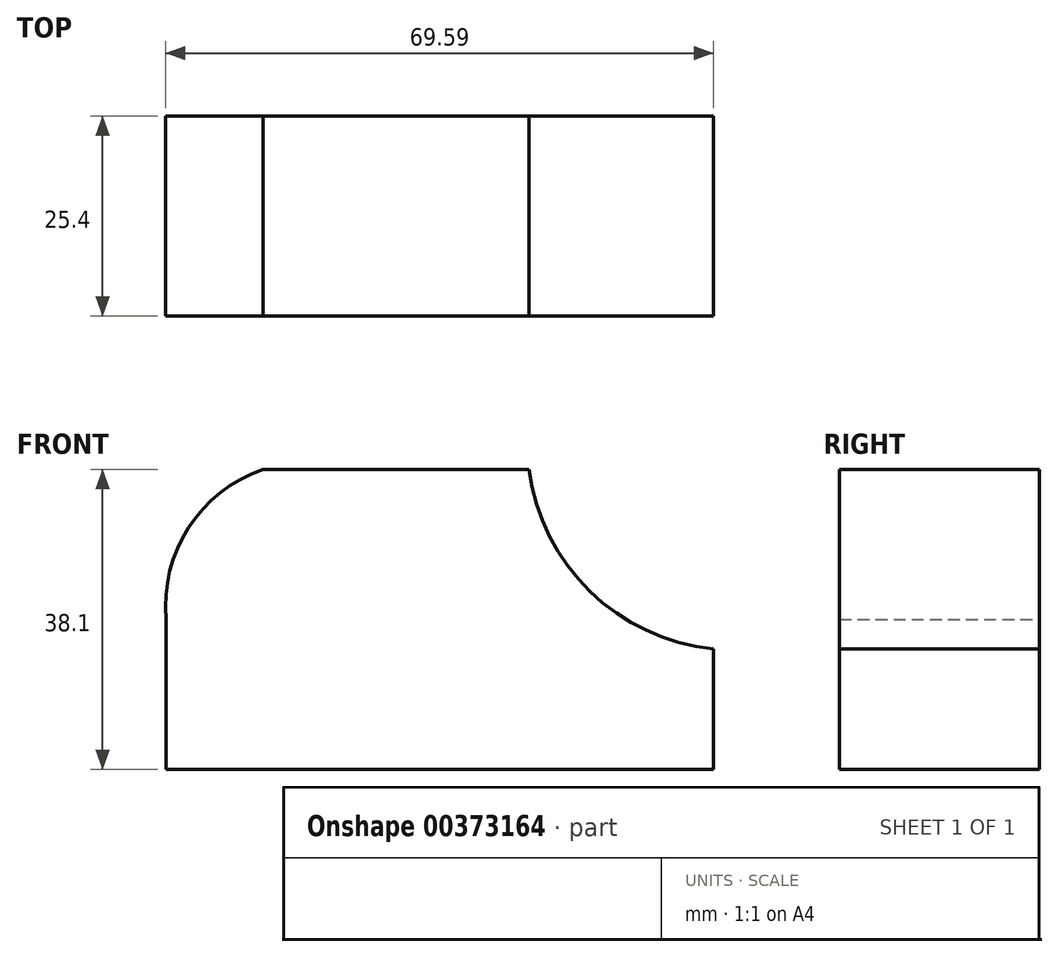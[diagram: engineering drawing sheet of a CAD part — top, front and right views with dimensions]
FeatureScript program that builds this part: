
annotation { "Feature Type Name" : "Feature", "Feature Type Description" : "" }
export const myFeature = defineFeature(function(context is Context, id is Id, definition is map)
    precondition{}
    {
        {
            var Q0;
            Q0=qCreatedBy(makeId("Front.planeOp"),FACE);
            var sketch = newSketch(context, id + "F0", { "sketchPlane" : qUnion([Q0])});
            skLineSegment(sketch, "E0", {"start": v(0, 0) * mm, "end": v(69.5, 0) * mm});
            skLineSegment(sketch, "E1", {"start": v(69.5, 0) * mm, "end": v(69.5, 38.1) * mm});
            skLineSegment(sketch, "E2", {"start": v(69.5, 38.1) * mm, "end": v(0, 38.1) * mm});
            skLineSegment(sketch, "E3", {"start": v(0, 38.1) * mm, "end": v(0, 0) * mm});
            skArc(sketch, "E4", {"start": v(12.28, 38.1) * mm, "mid": v(2.84, 30.7) * mm, "end": v(0, 19.05) * mm});
            skArc(sketch, "E5", {"start": v(46.11, 38.1) * mm, "mid": v(53.83, 22.62) * mm, "end": v(69.5, 15.32) * mm});
            skSolve(sketch);
        }
        {
            var Q0;
            {var subQ0=sQuery(id+"F0.wireOp",EDGE,"E4");var subQ1=sQuery(id+"F0.wireOp",EDGE,"E3");var subQ2=makeQuery(id+"F0.imprint","INTERSECT",VERTEX,{"disambiguationData":[OD(0.0)],"derivedFrom":[subQ1,subQ0]});Q0=makeQuery(id+"F0.imprint","IMPRINT",FACE,{"disambiguationData":[TD([[makeQuery(id+"F0.imprint","IMPRINT",EDGE,{"disambiguationData":[TD([[subQ2,1.0]])],"derivedFrom":subQ1}),-1.0]])]});}
            var Q1;
            {var subQ8=sQuery(id+"F0.wireOp",EDGE,"E0");Q1=makeQuery(id+"F0.imprint","IMPRINT",FACE,{"disambiguationData":[TD([[makeQuery(id+"F0.imprint","IMPRINT",EDGE,{"derivedFrom":subQ8}),1.0]])]});}
            extrude(context, id + "F1", {"entities" : qUnion([Q0, Q1]), "depth" : 25.4 * mm});
        }
    });
